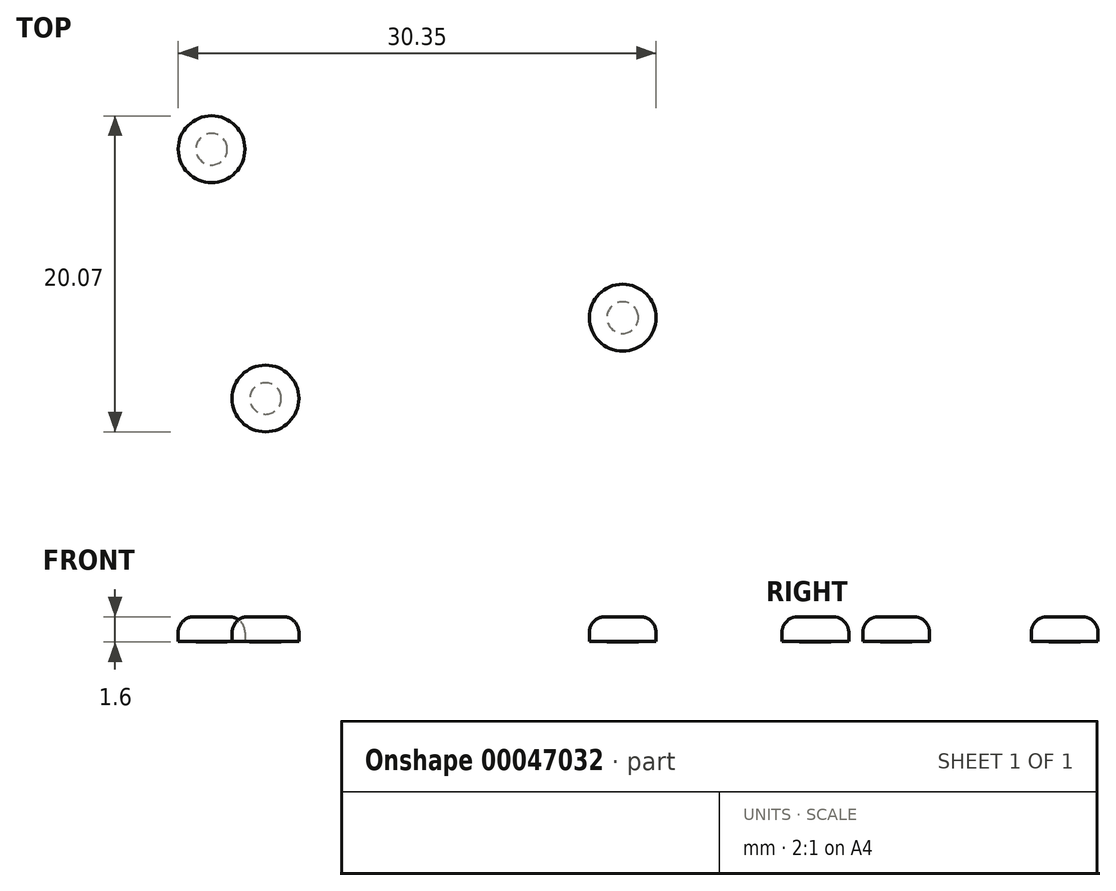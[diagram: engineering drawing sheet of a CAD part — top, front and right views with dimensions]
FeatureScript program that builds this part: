
annotation { "Feature Type Name" : "Feature", "Feature Type Description" : "" }
export const myFeature = defineFeature(function(context is Context, id is Id, definition is map)
    precondition{}
    {
        {
            var Q0;
            Q0=qCreatedBy(makeId("Top.planeOp"),FACE);
            var sketch = newSketch(context, id + "F0", { "sketchPlane" : qUnion([Q0])});
            skCircle(sketch, "E0", {"center": v(-47.37, 41.88) * mm, "radius": 2.12 * mm});
            skCircle(sketch, "E1", {"center": v(-43.95, 26.05) * mm, "radius": 2.12 * mm});
            skCircle(sketch, "E2", {"center": v(-21.26, 31.18) * mm, "radius": 2.12 * mm});
            skSolve(sketch);
        }
        {
            var Q0;
            Q0 = qSketchRegion(id + "F0", true);
            extrude(context, id + "F1", {"entities" : qUnion([Q0]), "depth" : 1.57 * mm});
        }
        {
            var Q0;
            Q0=makeQuery(id+"F1.opExtrude","CAP_EDGE",EDGE,{"disambiguationData":[OSD([sQuery(id+"F0.wireOp",EDGE,"E0")])],"isStart":false});
            var Q1;
            Q1=makeQuery(id+"F1.opExtrude","CAP_EDGE",EDGE,{"disambiguationData":[OSD([sQuery(id+"F0.wireOp",EDGE,"E1")])],"isStart":false});
            var Q2;
            Q2=makeQuery(id+"F1.opExtrude","CAP_EDGE",EDGE,{"disambiguationData":[OSD([sQuery(id+"F0.wireOp",EDGE,"E2")])],"isStart":false});
            fillet(context, id + "F2", {"entities" : qUnion([Q0, Q1, Q2]), "radius" : 1 * mm, "tangentPropagation" : true, "allowEdgeOverflow" : false});
        }
        {
            var Q0;
            Q0=makeQuery(id+"F1.opExtrude","CAP_FACE",FACE,{"disambiguationData":[OSD([sQuery(id+"F0.wireOp",EDGE,"E0")])],"isStart":true});
            var sketch = newSketch(context, id + "F3", { "sketchPlane" : qUnion([Q0])});
            skCircle(sketch, "E3", {"center": v(-47.37, -41.88) * mm, "radius": 1 * mm});
            skSolve(sketch);
        }
        {
            var Q0;
            Q0 = qSketchRegion(id + "F3", true);
            extrude(context, id + "F4", {"entities" : qUnion([Q0]), "operationType" : NewBodyOperationType.ADD, "depth" : 1 / 50.8 * mm});
        }
        {
            var Q0;
            Q0=makeQuery(id+"F1.opExtrude","CAP_FACE",FACE,{"disambiguationData":[OSD([sQuery(id+"F0.wireOp",EDGE,"E1")])],"isStart":true});
            var sketch = newSketch(context, id + "F5", { "sketchPlane" : qUnion([Q0])});
            skCircle(sketch, "E4", {"center": v(-43.95, -26.05) * mm, "radius": 1 * mm});
            skSolve(sketch);
        }
        {
            var Q0;
            Q0 = qSketchRegion(id + "F5", true);
            extrude(context, id + "F6", {"entities" : qUnion([Q0]), "operationType" : NewBodyOperationType.ADD, "depth" : 3 / 101.6 * mm});
        }
        {
            var Q0;
            Q0=makeQuery(id+"F1.opExtrude","CAP_FACE",FACE,{"disambiguationData":[OSD([sQuery(id+"F0.wireOp",EDGE,"E2")])],"isStart":true});
            var sketch = newSketch(context, id + "F7", { "sketchPlane" : qUnion([Q0])});
            skCircle(sketch, "E5", {"center": v(-21.26, -31.18) * mm, "radius": 1 * mm});
            skSolve(sketch);
        }
        {
            var Q0;
            Q0 = qSketchRegion(id + "F7", true);
            extrude(context, id + "F8", {"entities" : qUnion([Q0]), "operationType" : NewBodyOperationType.ADD, "depth" : 5 / 406.4 * mm});
        }
    });
